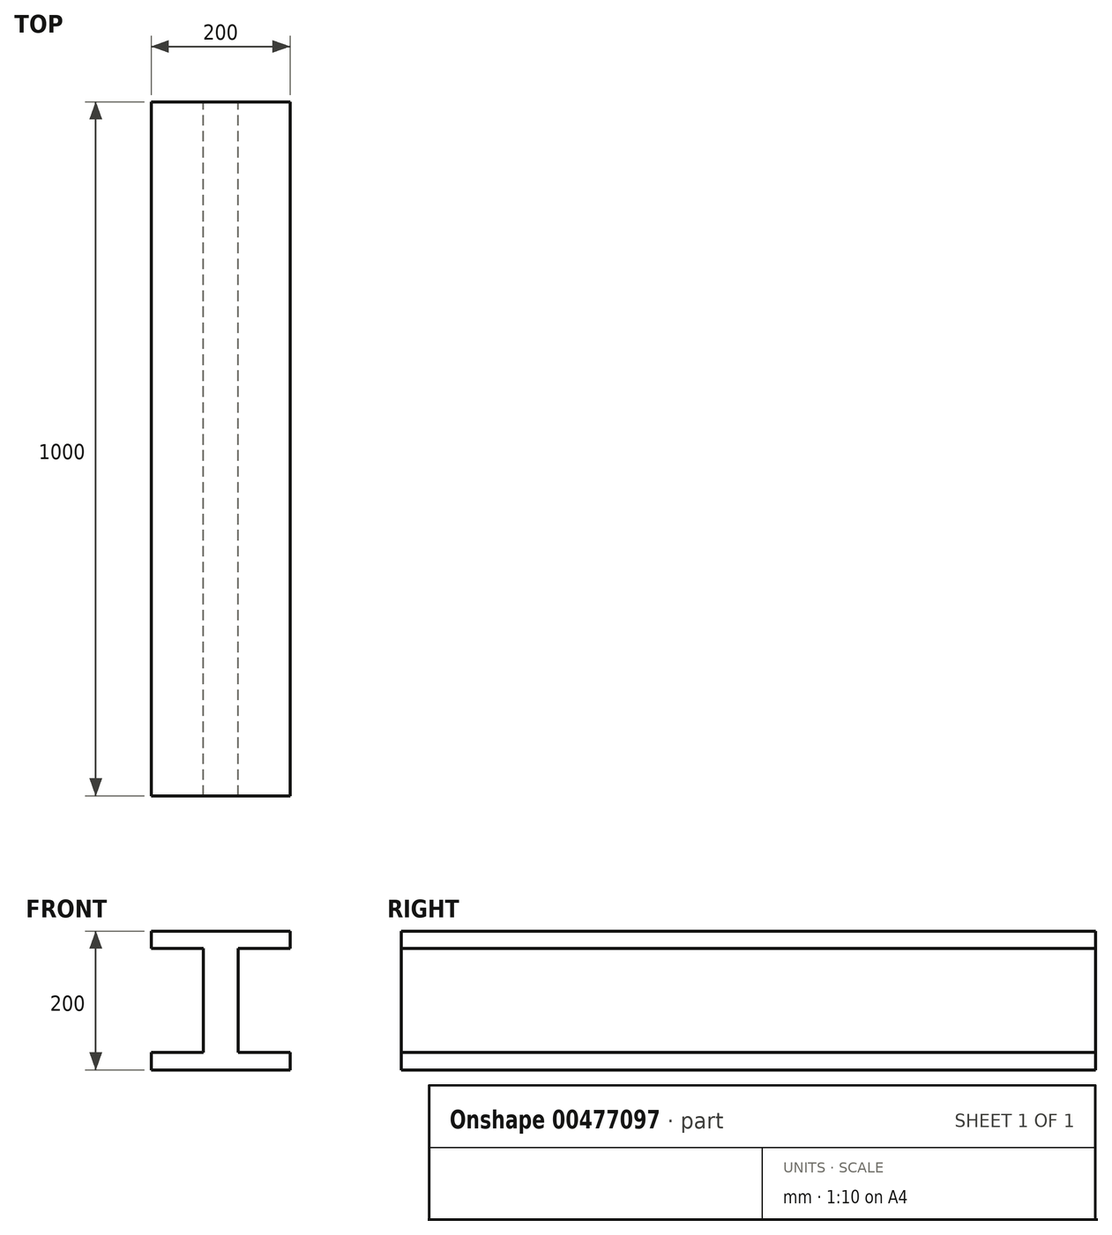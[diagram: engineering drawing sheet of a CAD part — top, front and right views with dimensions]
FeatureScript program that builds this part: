
annotation { "Feature Type Name" : "Feature", "Feature Type Description" : "" }
export const myFeature = defineFeature(function(context is Context, id is Id, definition is map)
    precondition{}
    {
        {
            var Q0;
            Q0=qCreatedBy(makeId("Front.planeOp"),FACE);
            var sketch = newSketch(context, id + "F0", { "sketchPlane" : qUnion([Q0])});
            skLineSegment(sketch, "E0", {"start": v(0, 100) * mm, "end": v(100, 100) * mm});
            skLineSegment(sketch, "E1", {"start": v(100, 100) * mm, "end": v(100, 75) * mm});
            skLineSegment(sketch, "E2", {"start": v(100, 75) * mm, "end": v(25, 75) * mm});
            skLineSegment(sketch, "E3", {"start": v(25, 75) * mm, "end": v(25, 0) * mm});
            skLineSegment(sketch, "E4", {"start": v(25, 0) * mm, "end": v(0, 0) * mm, "construction": true});
            skLineSegment(sketch, "E5", {"start": v(0, 100) * mm, "end": v(0, 0) * mm, "construction": true});
            skLineSegment(sketch, "E6.MirrorCS", {"start": v(0, -100) * mm, "end": v(100, -100) * mm});
            skLineSegment(sketch, "E7.MirrorCS", {"start": v(100, -100) * mm, "end": v(100, -75) * mm});
            skLineSegment(sketch, "E8.MirrorCS", {"start": v(100, -75) * mm, "end": v(25, -75) * mm});
            skLineSegment(sketch, "E9.MirrorCS", {"start": v(25, -75) * mm, "end": v(25, 0) * mm});
            skLineSegment(sketch, "E10.MirrorCS", {"start": v(0, -100) * mm, "end": v(0, 0) * mm, "construction": true});
            skLineSegment(sketch, "E11.MirrorCS", {"start": v(0, 100) * mm, "end": v(-100, 100) * mm});
            skLineSegment(sketch, "E12.MirrorCS", {"start": v(-100, 100) * mm, "end": v(-100, 75) * mm});
            skLineSegment(sketch, "E13.MirrorCS", {"start": v(-100, 75) * mm, "end": v(-25, 75) * mm});
            skLineSegment(sketch, "E14.MirrorCS", {"start": v(-25, 75) * mm, "end": v(-25, 0) * mm});
            skLineSegment(sketch, "E15.MirrorCS", {"start": v(-25, -75) * mm, "end": v(-25, 0) * mm});
            skLineSegment(sketch, "E16.MirrorCS", {"start": v(-100, -100) * mm, "end": v(-100, -75) * mm});
            skLineSegment(sketch, "E17.MirrorCS", {"start": v(0, -100) * mm, "end": v(-100, -100) * mm});
            skLineSegment(sketch, "E18.MirrorCS", {"start": v(-100, -75) * mm, "end": v(-25, -75) * mm});
            skSolve(sketch);
        }
        {
            var Q0;
            Q0=makeQuery(id+"F0.imprint","IMPRINT",FACE,{"disambiguationData":[TD([[makeQuery(id+"F0.imprint","IMPRINT",EDGE,{"derivedFrom":sQuery(id+"F0.wireOp",EDGE,"E0")}),-1.0]])]});
            extrude(context, id + "F1", {"entities" : qUnion([Q0]), "endBound" : BoundingType.SYMMETRIC, "depth" : 1000 * mm});
        }
    });
